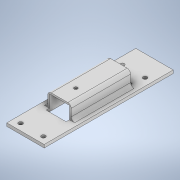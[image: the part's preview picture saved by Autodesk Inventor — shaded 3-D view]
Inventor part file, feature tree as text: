
AUTODESK INVENTOR PART (.ipt)
format: ipt  version: 2022 (Build 260153000, 153)  size: 269,312 bytes
history: native  units: in
note: dims shown in document units (in); Inventor stores cm internally (conversion verified against a paired STEP export)
features: extrude x6, sketch x6, fillet x2, projected_geometry x2
ambient origin geometry x8: Origin, YZ Plane, XZ Plane, XY Plane, X Axis, Y Axis, Z Axis, Center Point
bodies: Body1 (feature_tree)
feature tree (16):
  extrude  "Extrusion3"  Depth=0.0625in
  extrude  "Extrusion4"  Depth=0.0699in
  fillet  "Fillet1"  Radius=0.0699in
  extrude  "Extrusion5"  Depth=0.114in
  fillet  "Fillet2"  Radius=0.07in
  extrude  "Extrusion6"  Depth=0.07in
  extrude  "Extrusion7"  Depth=0.46in TaperAngle=0.0deg
  extrude  "Extrusion8"  Depth=0.0625in TaperAngle=0.0deg
  sketch  "Sketch1"  dims[d0=0.003in d1=0.0625in d2=0.15in d3=4.2322in d4=6.13in]
  sketch  "Sketch2"  dims[d5=0.0699in d6=0.0699in d7=0.0699in]
  sketch  "Sketch3"  dims[d12=0.114in d13=0.0in d14=0.07in d15=0.07in]
  sketch  "Sketch4"  dims[d16=0.07in d17=0.07in]
  projected_geometry  "Projected Loop1"
  sketch  "Sketch5"  dims[d18=0.0625in d19=0.46in d20=0.0in]
  sketch  "Sketch6"  dims[d21=0.125in d22=0.0625in d23=0.0in d24=0.125in d25=0.125in d26=0.0in d27=0.3075in d28=0.3075in d29=0.125in d30=0.0in d31=0.6in d32=0.125in d33=0.125in d34=0.0in]
  projected_geometry  "Projected Loop2"
